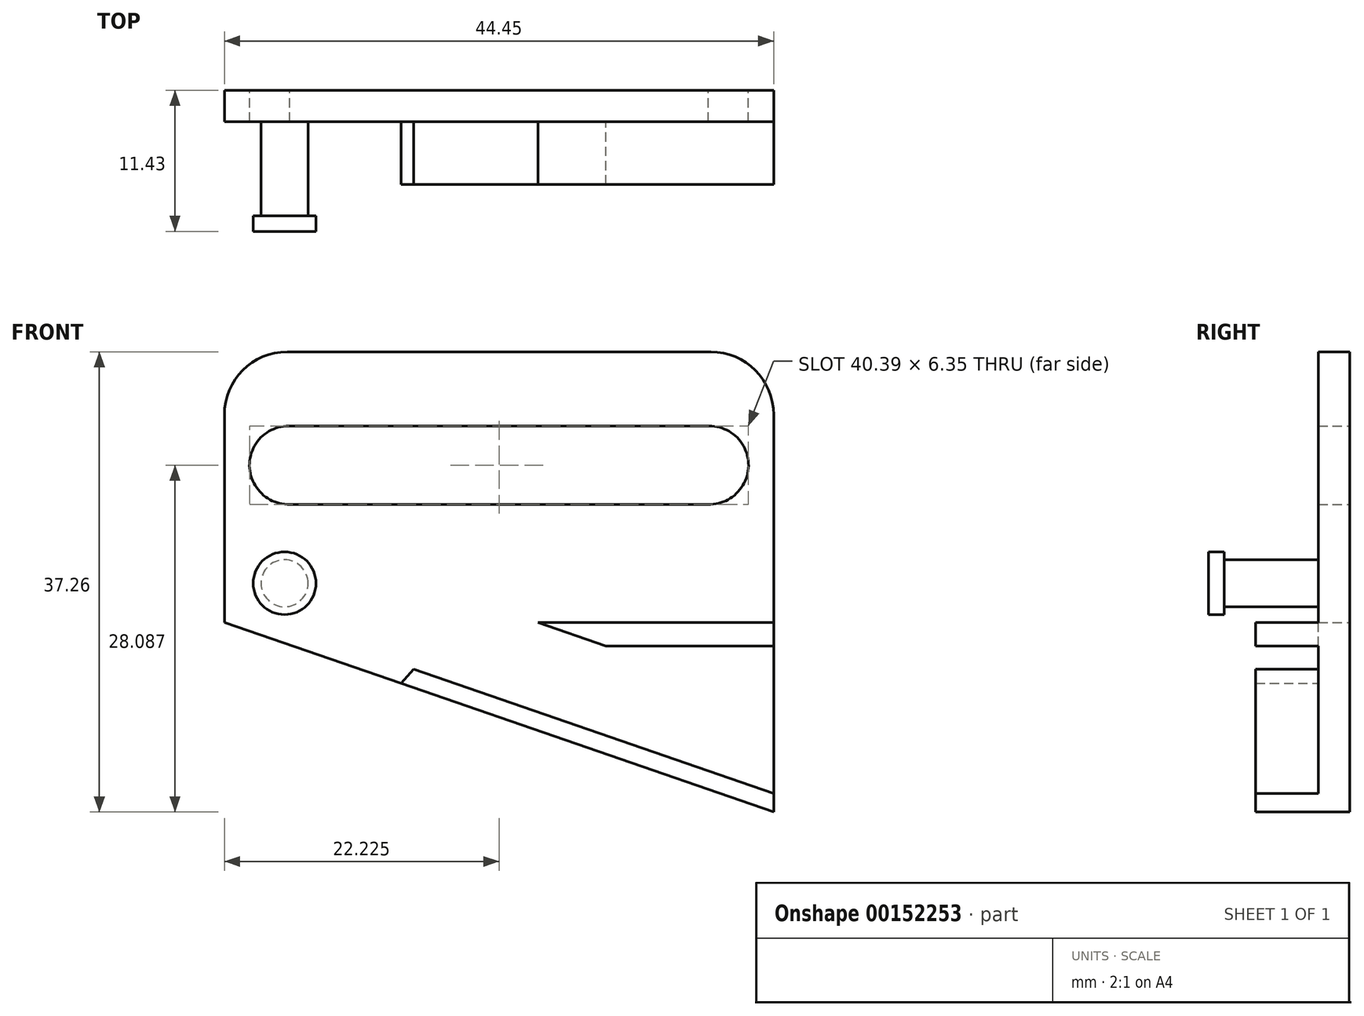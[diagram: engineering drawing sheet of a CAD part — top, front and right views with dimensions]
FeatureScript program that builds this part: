
annotation { "Feature Type Name" : "Feature", "Feature Type Description" : "" }
export const myFeature = defineFeature(function(context is Context, id is Id, definition is map)
    precondition{}
    {
        {
            var Q0;
            Q0=qCreatedBy(makeId("Front.planeOp"),FACE);
            var sketch = newSketch(context, id + "F0", { "sketchPlane" : qUnion([Q0])});
            skLineSegment(sketch, "E0", {"start": v(27.49, 0) * mm, "end": v(44.45, 0) * mm});
            skLineSegment(sketch, "E1", {"start": v(44.45, 0) * mm, "end": v(44.45, 21.9) * mm});
            skLineSegment(sketch, "E2", {"start": v(44.45, 21.9) * mm, "end": v(0, 21.9) * mm});
            skLineSegment(sketch, "E3", {"start": v(0, 21.9) * mm, "end": v(0, 0) * mm});
            skLineSegment(sketch, "E4", {"start": v(0, 0) * mm, "end": v(12.7, -30.69) * mm});
            skLineSegment(sketch, "E5", {"start": v(12.7, -30.69) * mm, "end": v(36.17, -20.97) * mm});
            skLineSegment(sketch, "E6", {"start": v(36.17, -20.97) * mm, "end": v(27.49, 0) * mm});
            skPoint(sketch, "E7", {"position": v(22.23, 13.44) * mm});
            skPoint(sketch, "E8", {"position": v(22.23, 21.9) * mm});
            skCircle(sketch, "E9", {"center": v(5.2, 12.74) * mm, "radius": 3.18 * mm});
            skCircle(sketch, "E10", {"center": v(39.24, 12.74) * mm, "radius": 3.18 * mm});
            skLineSegment(sketch, "E11", {"start": v(5.2, 15.91) * mm, "end": v(39.24, 15.91) * mm});
            skLineSegment(sketch, "E12", {"start": v(5.3, 9.56) * mm, "end": v(39.34, 9.56) * mm});
            skSolve(sketch);
        }
        {
            var Q0;
            Q0=makeQuery(id+"F0.imprint","IMPRINT",FACE,{"disambiguationData":[TD([[makeQuery(id+"F0.imprint","IMPRINT",EDGE,{"derivedFrom":sQuery(id+"F0.wireOp",EDGE,"E0")}),1.0]])]});
            extrude(context, id + "F1", {"entities" : qUnion([Q0]), "depth" : 2.54 * mm});
        }
        {
            var Q0;
            Q0=makeQuery(id+"F1.opExtrude","SWEPT_EDGE",EDGE,{"disambiguationData":[OSD([sQuery(id+"F0.wireOp",EDGE,"E2"),sQuery(id+"F0.wireOp",EDGE,"E3")])]});
            var Q1;
            Q1=makeQuery(id+"F1.opExtrude","SWEPT_EDGE",EDGE,{"disambiguationData":[OSD([sQuery(id+"F0.wireOp",EDGE,"E1"),sQuery(id+"F0.wireOp",EDGE,"E2")])]});
            fillet(context, id + "F2", {"entities" : qUnion([Q0, Q1]), "radius" : 5.08 * mm, "tangentPropagation" : true, "allowEdgeOverflow" : false});
        }
        {
            var Q0;
            Q0=makeQuery(id+"F1.opExtrude","CAP_FACE",FACE,{"disambiguationData":[OSD([sQuery(id+"F0.wireOp",EDGE,"E0"),sQuery(id+"F0.wireOp",EDGE,"E1"),sQuery(id+"F0.wireOp",EDGE,"E2"),sQuery(id+"F0.wireOp",EDGE,"E3"),sQuery(id+"F0.wireOp",EDGE,"E4"),sQuery(id+"F0.wireOp",EDGE,"E5"),sQuery(id+"F0.wireOp",EDGE,"E6"),sQuery(id+"F0.wireOp",EDGE,"EWFZg2cJ-M6Fa-qDMC-XPxy-4REUc7ZFGAs4.bottom"),sQuery(id+"F0.wireOp",EDGE,"EWFZg2cJ-M6Fa-qDMC-XPxy-4REUc7ZFGAs4.top"),sQuery(id+"F0.wireOp",EDGE,"R0JTWTLm-udwL-i8by-LiGk-pPOAkAqr1kJQ"),sQuery(id+"F0.wireOp",EDGE,"P9WVeyoa-iMAh-U4rP-Lq8l-UnnVuXTkSbAP")])],"isStart":false});
            var sketch = newSketch(context, id + "F3", { "sketchPlane" : qUnion([Q0])});
            skLineSegment(sketch, "E13.0", {"start": v(2.75, 0) * mm, "end": v(15.05, -29.72) * mm});
            skLineSegment(sketch, "E14", {"start": v(0, 0) * mm, "end": v(2.75, 0) * mm});
            skSolve(sketch);
        }
        {
            var Q0;
            {var subQ0=sQuery(id+"F3.wireOp",EDGE,"E13.0");Q0=makeQuery(id+"F3.imprint","IMPRINT",FACE,{"disambiguationData":[TD([[makeQuery(id+"F3.imprint","IMPRINT",EDGE,{"derivedFrom":subQ0}),-1.0]])]});}
            extrude(context, id + "F4", {"entities" : qUnion([Q0]), "operationType" : NewBodyOperationType.ADD, "depth" : 6.35 * mm});
        }
        {
            var Q0;
            Q0=makeQuery(id+"F1.opExtrude","CAP_FACE",FACE,{"disambiguationData":[OSD([sQuery(id+"F0.wireOp",EDGE,"E0"),sQuery(id+"F0.wireOp",EDGE,"E1"),sQuery(id+"F0.wireOp",EDGE,"E2"),sQuery(id+"F0.wireOp",EDGE,"E3"),sQuery(id+"F0.wireOp",EDGE,"E4"),sQuery(id+"F0.wireOp",EDGE,"E5"),sQuery(id+"F0.wireOp",EDGE,"E6"),sQuery(id+"F0.wireOp",EDGE,"EWFZg2cJ-M6Fa-qDMC-XPxy-4REUc7ZFGAs4.bottom"),sQuery(id+"F0.wireOp",EDGE,"EWFZg2cJ-M6Fa-qDMC-XPxy-4REUc7ZFGAs4.top"),sQuery(id+"F0.wireOp",EDGE,"R0JTWTLm-udwL-i8by-LiGk-pPOAkAqr1kJQ"),sQuery(id+"F0.wireOp",EDGE,"P9WVeyoa-iMAh-U4rP-Lq8l-UnnVuXTkSbAP")])],"isStart":false});
            var sketch = newSketch(context, id + "F5", { "sketchPlane" : qUnion([Q0])});
            skLineSegment(sketch, "E15", {"start": v(20.91, -27.29) * mm, "end": v(-0.63, 24.78) * mm, "construction": true});
            skLineSegment(sketch, "E16.0", {"start": v(2.75, 0) * mm, "end": v(15.05, -29.72) * mm});
            skLineSegment(sketch, "E17", {"start": v(2.75, 0) * mm, "end": v(-6.68, 22.78) * mm, "construction": true});
            skLineSegment(sketch, "E18", {"start": v(17.98, -28.5) * mm, "end": v(6.19, 0) * mm, "construction": true});
            skLineSegment(sketch, "E19", {"start": v(2.75, 0) * mm, "end": v(54.96, 0) * mm, "construction": true});
            skLineSegment(sketch, "E20", {"start": v(-1.85, 6.35) * mm, "end": v(54.8, 6.35) * mm, "construction": true});
            skLineSegment(sketch, "E21", {"start": v(0.12, 6.35) * mm, "end": v(9.62, 0) * mm, "construction": true});
            skLineSegment(sketch, "E22", {"start": v(2.75, 0) * mm, "end": v(7, 6.35) * mm, "construction": true});
            skCircle(sketch, "E23", {"center": v(4.87, 3.17) * mm, "radius": 3.17 * mm, "construction": true});
            skCircle(sketch, "E24", {"center": v(4.87, 3.17) * mm, "radius": 1.9 * mm});
            skSolve(sketch);
        }
        {
            var Q0;
            Q0=makeQuery(id+"F5.imprint","IMPRINT",FACE,{"disambiguationData":[TD([[makeQuery(id+"F5.imprint","IMPRINT",EDGE,{"derivedFrom":sQuery(id+"F5.wireOp",EDGE,"E24")}),1.0]])]});
            extrude(context, id + "F6", {"entities" : qUnion([Q0]), "operationType" : NewBodyOperationType.ADD, "depth" : 6.35 * mm});
        }
        {
            var Q0;
            Q0=makeQuery(id+"F4.opExtrude","CAP_FACE",FACE,{"disambiguationData":[OSD([sQuery(id+"F0.wireOp",EDGE,"E4"),sQuery(id+"F0.wireOp",EDGE,"E5"),sQuery(id+"F3.wireOp",EDGE,"E13.0"),sQuery(id+"F3.wireOp",EDGE,"E14")])],"isStart":false});
            extrude(context, id + "F7", {"entities" : qUnion([Q0]), "operationType" : NewBodyOperationType.ADD, "depth" : 2.54 * mm});
        }
        {
            var Q0;
            Q0=makeQuery(id+"F6.opExtrude","CAP_FACE",FACE,{"disambiguationData":[OSD([sQuery(id+"F5.wireOp",EDGE,"E24")])],"isStart":false});
            extrude(context, id + "F8", {"entities" : qUnion([Q0]), "operationType" : NewBodyOperationType.ADD, "depth" : 2.54 * mm});
        }
        {
            var Q0;
            Q0=makeQuery(id+"F1.opExtrude","CAP_FACE",FACE,{"disambiguationData":[OSD([sQuery(id+"F0.wireOp",EDGE,"E0"),sQuery(id+"F0.wireOp",EDGE,"E1"),sQuery(id+"F0.wireOp",EDGE,"E2"),sQuery(id+"F0.wireOp",EDGE,"E3"),sQuery(id+"F0.wireOp",EDGE,"E4"),sQuery(id+"F0.wireOp",EDGE,"E5"),sQuery(id+"F0.wireOp",EDGE,"E6"),sQuery(id+"F0.wireOp",EDGE,"EWFZg2cJ-M6Fa-qDMC-XPxy-4REUc7ZFGAs4.bottom"),sQuery(id+"F0.wireOp",EDGE,"EWFZg2cJ-M6Fa-qDMC-XPxy-4REUc7ZFGAs4.top"),sQuery(id+"F0.wireOp",EDGE,"R0JTWTLm-udwL-i8by-LiGk-pPOAkAqr1kJQ"),sQuery(id+"F0.wireOp",EDGE,"P9WVeyoa-iMAh-U4rP-Lq8l-UnnVuXTkSbAP")])],"isStart":false});
            var sketch = newSketch(context, id + "F9", { "sketchPlane" : qUnion([Q0])});
            skCircle(sketch, "E25", {"center": v(4.87, 3.17) * mm, "radius": 2.54 * mm});
            skSolve(sketch);
        }
        {
            var Q0;
            Q0=makeQuery(id+"F9.imprint","IMPRINT",FACE,{"disambiguationData":[TD([[makeQuery(id+"F9.imprint","IMPRINT",EDGE,{"derivedFrom":sQuery(id+"F9.wireOp",EDGE,"E25")}),1.0]])]});
            extrude(context, id + "F10", {"entities" : qUnion([Q0]), "operationType" : NewBodyOperationType.ADD, "depth" : 8.9 * mm, "hasSecondDirection" : true, "secondDirectionOppositeDirection" : false, "secondDirectionDepth" : 7.62 * mm});
        }
        {
            var Q0;
            Q0=makeQuery(id+"F1.opExtrude","CAP_FACE",FACE,{"disambiguationData":[OSD([sQuery(id+"F0.wireOp",EDGE,"E0"),sQuery(id+"F0.wireOp",EDGE,"E1"),sQuery(id+"F0.wireOp",EDGE,"E2"),sQuery(id+"F0.wireOp",EDGE,"E3"),sQuery(id+"F0.wireOp",EDGE,"E4"),sQuery(id+"F0.wireOp",EDGE,"E5"),sQuery(id+"F0.wireOp",EDGE,"E6"),sQuery(id+"F0.wireOp",EDGE,"EWFZg2cJ-M6Fa-qDMC-XPxy-4REUc7ZFGAs4.bottom"),sQuery(id+"F0.wireOp",EDGE,"EWFZg2cJ-M6Fa-qDMC-XPxy-4REUc7ZFGAs4.top"),sQuery(id+"F0.wireOp",EDGE,"R0JTWTLm-udwL-i8by-LiGk-pPOAkAqr1kJQ"),sQuery(id+"F0.wireOp",EDGE,"P9WVeyoa-iMAh-U4rP-Lq8l-UnnVuXTkSbAP")])],"isStart":false});
            var sketch = newSketch(context, id + "F11", { "sketchPlane" : qUnion([Q0])});
            skLineSegment(sketch, "E26", {"start": v(44.45, 0) * mm, "end": v(27.49, 0) * mm});
            skLineSegment(sketch, "E27", {"start": v(44.45, 0) * mm, "end": v(44.45, -2.54) * mm});
            skLineSegment(sketch, "E28", {"start": v(44.45, -2.54) * mm, "end": v(28.54, -2.54) * mm});
            skLineSegment(sketch, "E29", {"start": v(28.54, -2.54) * mm, "end": v(27.49, 0) * mm});
            skSolve(sketch);
        }
        {
            var Q0;
            Q0=makeQuery(id+"F11.imprint","IMPRINT",FACE,{"disambiguationData":[TD([[makeQuery(id+"F11.imprint","IMPRINT",EDGE,{"derivedFrom":sQuery(id+"F11.wireOp",EDGE,"E27")}),-1.0]])]});
            extrude(context, id + "F12", {"entities" : qUnion([Q0]), "operationType" : NewBodyOperationType.ADD, "oppositeDirection" : true, "depth" : 2.54 * mm, "hasSecondDirection" : true, "secondDirectionOppositeDirection" : false, "secondDirectionDepth" : 6.35 * mm});
        }
        {
            var Q0;
            {var subQ0=sQuery(id+"F5.wireOp",EDGE,"E24");Q0=makeQuery(id+"F10.boolean.opBoolean","MERGE",FACE,{"derivedFrom":[makeQuery(id+"F8.opExtrude","CAP_FACE",FACE,{"disambiguationData":[OSD([subQ0])],"isStart":false}),makeQuery(id+"F10.opExtrude","CAP_FACE",FACE,{"disambiguationData":[OSD([subQ0,sQuery(id+"F9.wireOp",EDGE,"E25")])],"isStart":false})]});}
            var sketch = newSketch(context, id + "F13", { "sketchPlane" : qUnion([Q0])});
            skCircle(sketch, "E30.0", {"center": v(4.87, 3.17) * mm, "radius": 1.9 * mm});
            skCircle(sketch, "E31", {"center": v(4.87, 3.17) * mm, "radius": 3.81 * mm, "construction": true});
            skPoint(sketch, "E32", {"position": v(2.75, 0) * mm});
            skLineSegment(sketch, "E33", {"start": v(4.87, 3.17) * mm, "end": v(57.45, 3.17) * mm, "construction": true});
            skLineSegment(sketch, "E34", {"start": v(6.98, 0) * mm, "end": v(58.06, 0) * mm, "construction": true});
            skLineSegment(sketch, "E35.MirrorCS", {"start": v(6.98, 6.35) * mm, "end": v(58.06, 6.35) * mm, "construction": true});
            skSolve(sketch);
        }
        {
            var Q0;
            Q0=makeQuery(id+"F0.imprint","IMPRINT",FACE,{"disambiguationData":[TD([[makeQuery(id+"F0.imprint","IMPRINT",EDGE,{"derivedFrom":sQuery(id+"F0.wireOp",EDGE,"E0")}),1.0]])]});
            var sketch = newSketch(context, id + "F14", { "sketchPlane" : qUnion([Q0])});
            skLineSegment(sketch, "E36.bottom", {"start": v(0, 0) * mm, "end": v(44.45, 0) * mm});
            skLineSegment(sketch, "E36.top", {"start": v(0, -31.1) * mm, "end": v(44.45, -31.1) * mm});
            skLineSegment(sketch, "E36.left", {"start": v(0, 0) * mm, "end": v(0, -31.1) * mm});
            skLineSegment(sketch, "E36.right", {"start": v(44.45, 0) * mm, "end": v(44.45, -31.1) * mm});
            skSolve(sketch);
        }
        {
            var Q0;
            Q0=makeQuery(id+"F14.imprint","IMPRINT",FACE,{"disambiguationData":[TD([[makeQuery(id+"F14.imprint","IMPRINT",EDGE,{"derivedFrom":sQuery(id+"F14.wireOp",EDGE,"E36.top")}),1.0]])]});
            var Q1;
            {var subQ2=makeQuery(id+"F0.imprint","IMPRINT",EDGE,{"derivedFrom":sQuery(id+"F0.wireOp",EDGE,"E4")});Q1=makeQuery(id+"F14.imprint","IMPRINT",FACE,{"disambiguationData":[TD([[makeQuery(id+"F14.imprint","IMPRINT",EDGE,{"derivedFrom":subQ2}),1.0]])]});}
            extrude(context, id + "F15", {"entities" : qUnion([Q0, Q1]), "operationType" : NewBodyOperationType.REMOVE, "depth" : 25.4 * mm});
        }
        {
            var Q0;
            Q0=qCreatedBy(makeId("Front.planeOp"),FACE);
            var sketch = newSketch(context, id + "F16", { "sketchPlane" : qUnion([Q0])});
            skLineSegment(sketch, "E37.0", {"start": v(44.45, 0) * mm, "end": v(44.45, 16.83) * mm});
            skLineSegment(sketch, "E38.0", {"start": v(6.98, 0) * mm, "end": v(21.59, 0) * mm, "construction": true});
            skLineSegment(sketch, "E39.bottom", {"start": v(44.45, 0) * mm, "end": v(21.59, 0) * mm});
            skLineSegment(sketch, "E39.top", {"start": v(44.45, -1.9) * mm, "end": v(30.89, -1.9) * mm});
            skLineSegment(sketch, "E39.left", {"start": v(44.45, 0) * mm, "end": v(44.45, -1.9) * mm});
            skLineSegment(sketch, "E40", {"start": v(0, 0) * mm, "end": v(44.45, -15.35) * mm});
            skLineSegment(sketch, "E41", {"start": v(44.45, -13.85) * mm, "end": v(15.3, -3.8) * mm});
            skLineSegment(sketch, "E42", {"start": v(15.3, -3.8) * mm, "end": v(14.3, -4.94) * mm});
            skPoint(sketch, "E43.0", {"position": v(4.87, 3.17) * mm});
            skLineSegment(sketch, "E44", {"start": v(4.87, 3.18) * mm, "end": v(54.66, -14.01) * mm, "construction": true});
            skLineSegment(sketch, "E45.0", {"start": v(6.98, 6.35) * mm, "end": v(58.06, 6.35) * mm, "construction": true});
            skLineSegment(sketch, "E46.0", {"start": v(4.87, 3.17) * mm, "end": v(57.45, 3.17) * mm, "construction": true});
            skLineSegment(sketch, "E47", {"start": v(6.98, 6.35) * mm, "end": v(30.89, -1.9) * mm, "construction": true});
            skCircle(sketch, "E48.0", {"center": v(4.87, 3.17) * mm, "radius": 3.81 * mm, "construction": true});
            skLineSegment(sketch, "E49.trimOffspring", {"start": v(25.37, 0) * mm, "end": v(58.06, 0) * mm, "construction": true});
            skLineSegment(sketch, "E50", {"start": v(25.37, 0) * mm, "end": v(30.89, -1.9) * mm});
            skLineSegment(sketch, "E51", {"start": v(44.45, -1.9) * mm, "end": v(44.45, -15.35) * mm});
            skLineSegment(sketch, "E52.trimOffspring", {"start": v(44.45, -6.59) * mm, "end": v(57.79, -11.2) * mm, "construction": true});
            skLineSegment(sketch, "E53", {"start": v(0, 0) * mm, "end": v(25.37, 0) * mm});
            skSolve(sketch);
        }
        {
            var Q0;
            Q0 = qSketchRegion(id + "F16", true);
            extrude(context, id + "F17", {"entities" : qUnion([Q0]), "operationType" : NewBodyOperationType.ADD, "depth" : 2.54 * mm});
        }
        {
            var Q0;
            Q0=makeQuery(id+"F16.imprint","IMPRINT",FACE,{"disambiguationData":[TD([[makeQuery(id+"F16.imprint","IMPRINT",EDGE,{"derivedFrom":sQuery(id+"F16.wireOp",EDGE,"E39.bottom")}),1.0]])]});
            var Q1;
            {var subQ4=sQuery(id+"F16.wireOp",EDGE,"E41");Q1=makeQuery(id+"F16.imprint","IMPRINT",FACE,{"disambiguationData":[TD([[makeQuery(id+"F16.imprint","IMPRINT",EDGE,{"derivedFrom":subQ4}),1.0]])]});}
            extrude(context, id + "F18", {"entities" : qUnion([Q0, Q1]), "operationType" : NewBodyOperationType.ADD, "depth" : 7.62 * mm});
        }
    });
